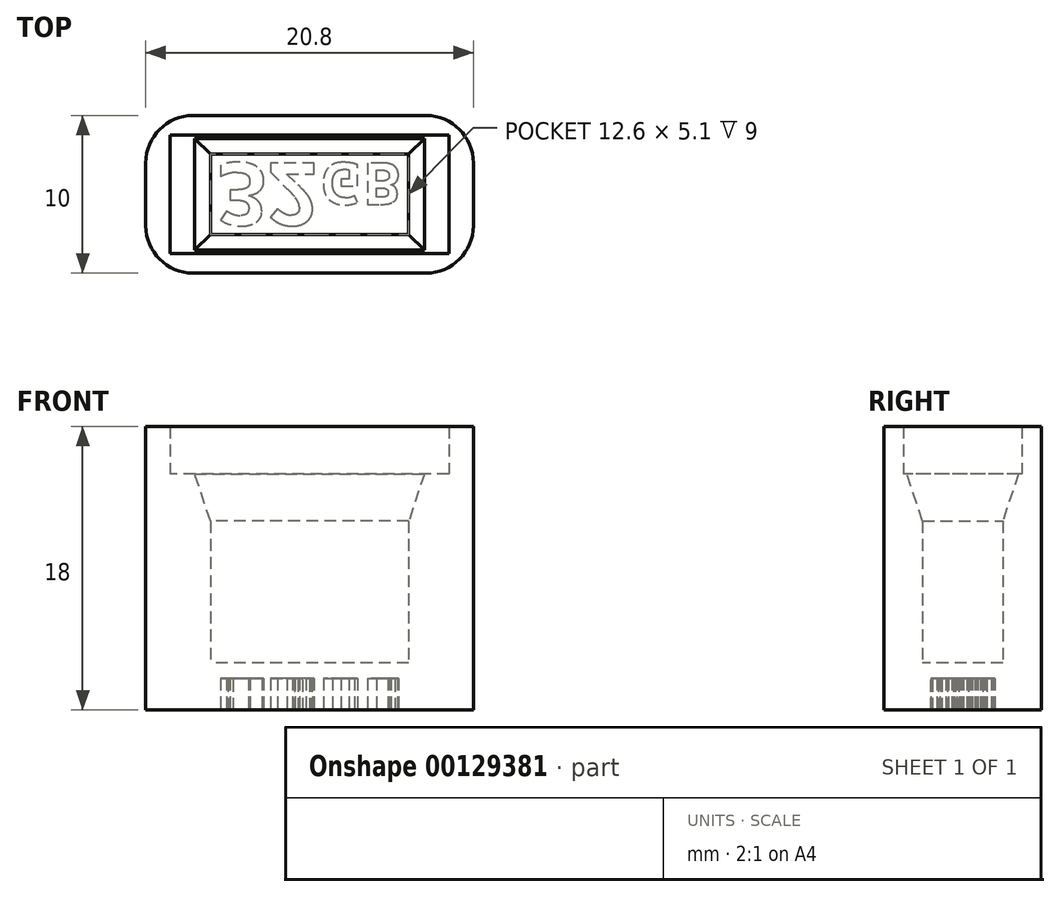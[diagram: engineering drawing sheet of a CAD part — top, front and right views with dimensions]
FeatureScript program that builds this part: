
annotation { "Feature Type Name" : "Feature", "Feature Type Description" : "" }
export const myFeature = defineFeature(function(context is Context, id is Id, definition is map)
    precondition{}
    {
        {
            var Q0;
            Q0=qCreatedBy(makeId("Top.planeOp"),FACE);
            var sketch = newSketch(context, id + "F0", { "sketchPlane" : qUnion([Q0])});
            skLineSegment(sketch, "E0.bottom", {"start": v(10.4, 5) * mm, "end": v(-10.4, 5) * mm});
            skLineSegment(sketch, "E0.top", {"start": v(10.4, -5) * mm, "end": v(-10.4, -5) * mm});
            skLineSegment(sketch, "E0.left", {"start": v(10.4, 5) * mm, "end": v(10.4, -5) * mm});
            skLineSegment(sketch, "E0.right", {"start": v(-10.4, 5) * mm, "end": v(-10.4, -5) * mm});
            skPoint(sketch, "E0.middle", {"position": v(0, 0) * mm});
            skLineSegment(sketch, "E1.bottom", {"start": v(8.85, 3.75) * mm, "end": v(-8.85, 3.75) * mm});
            skLineSegment(sketch, "E1.top", {"start": v(8.85, -3.75) * mm, "end": v(-8.85, -3.75) * mm});
            skLineSegment(sketch, "E1.left", {"start": v(8.85, 3.75) * mm, "end": v(8.85, -3.75) * mm});
            skLineSegment(sketch, "E1.right", {"start": v(-8.85, 3.75) * mm, "end": v(-8.85, -3.75) * mm});
            skSolve(sketch);
        }
        {
            var Q0;
            Q0=makeQuery(id+"F0.imprint","IMPRINT",FACE,{"disambiguationData":[TD([[makeQuery(id+"F0.imprint","IMPRINT",EDGE,{"derivedFrom":sQuery(id+"F0.wireOp",EDGE,"E0.bottom")}),1.0]])]});
            extrude(context, id + "F1", {"entities" : qUnion([Q0]), "depth" : 15 * mm});
        }
        {
            var Q0;
            Q0=makeQuery(id+"F0.imprint","IMPRINT",FACE,{"disambiguationData":[TD([[makeQuery(id+"F0.imprint","IMPRINT",EDGE,{"derivedFrom":sQuery(id+"F0.wireOp",EDGE,"E1.bottom")}),1.0]])]});
            var Q1;
            Q1=makeQuery(id+"F0.imprint","IMPRINT",FACE,{"disambiguationData":[TD([[makeQuery(id+"F0.imprint","IMPRINT",EDGE,{"derivedFrom":sQuery(id+"F0.wireOp",EDGE,"E0.bottom")}),1.0]])]});
            extrude(context, id + "F2", {"entities" : qUnion([Q0, Q1]), "operationType" : NewBodyOperationType.ADD, "oppositeDirection" : true, "depth" : 3 * mm});
        }
        {
            var Q0;
            {var subQ0=sQuery(id+"F0.wireOp",EDGE,"E0.right");var subQ1=sQuery(id+"F0.wireOp",EDGE,"E0.top");Q0=makeQuery(id+"F2.boolean.opBoolean","MERGE",EDGE,{"derivedFrom":[makeQuery(id+"F1.opExtrude","SWEPT_EDGE",EDGE,{"disambiguationData":[OSD([subQ1,subQ0])]}),makeQuery(id+"F2.opExtrude","SWEPT_EDGE",EDGE,{"disambiguationData":[OSD([subQ1,subQ0])]})]});}
            var Q1;
            {var subQ0=sQuery(id+"F0.wireOp",EDGE,"E0.right");var subQ1=sQuery(id+"F0.wireOp",EDGE,"E0.bottom");Q1=makeQuery(id+"F2.boolean.opBoolean","MERGE",EDGE,{"derivedFrom":[makeQuery(id+"F1.opExtrude","SWEPT_EDGE",EDGE,{"disambiguationData":[OSD([subQ1,subQ0])]}),makeQuery(id+"F2.opExtrude","SWEPT_EDGE",EDGE,{"disambiguationData":[OSD([subQ1,subQ0])]})]});}
            var Q2;
            {var subQ0=sQuery(id+"F0.wireOp",EDGE,"E0.left");var subQ1=sQuery(id+"F0.wireOp",EDGE,"E0.bottom");Q2=makeQuery(id+"F2.boolean.opBoolean","MERGE",EDGE,{"derivedFrom":[makeQuery(id+"F1.opExtrude","SWEPT_EDGE",EDGE,{"disambiguationData":[OSD([subQ1,subQ0])]}),makeQuery(id+"F2.opExtrude","SWEPT_EDGE",EDGE,{"disambiguationData":[OSD([subQ1,subQ0])]})]});}
            var Q3;
            {var subQ0=sQuery(id+"F0.wireOp",EDGE,"E0.left");var subQ1=sQuery(id+"F0.wireOp",EDGE,"E0.top");Q3=makeQuery(id+"F2.boolean.opBoolean","MERGE",EDGE,{"derivedFrom":[makeQuery(id+"F1.opExtrude","SWEPT_EDGE",EDGE,{"disambiguationData":[OSD([subQ1,subQ0])]}),makeQuery(id+"F2.opExtrude","SWEPT_EDGE",EDGE,{"disambiguationData":[OSD([subQ1,subQ0])]})]});}
            fillet(context, id + "F3", {"entities" : qUnion([Q0, Q1, Q2, Q3]), "radius" : 3 * mm, "tangentPropagation" : true, "allowEdgeOverflow" : false});
        }
        {
            var Q0;
            Q0=makeQuery(id+"F2.opExtrude","CAP_FACE",FACE,{"disambiguationData":[OSD([sQuery(id+"F0.wireOp",EDGE,"E0.bottom"),sQuery(id+"F0.wireOp",EDGE,"E0.top"),sQuery(id+"F0.wireOp",EDGE,"E0.left"),sQuery(id+"F0.wireOp",EDGE,"E0.right")])],"isStart":true});
            var sketch = newSketch(context, id + "F4", { "sketchPlane" : qUnion([Q0])});
            skLineSegment(sketch, "E2.bottom", {"start": v(6.3, 2.55) * mm, "end": v(-6.3, 2.55) * mm});
            skLineSegment(sketch, "E2.top", {"start": v(6.3, -2.55) * mm, "end": v(-6.3, -2.55) * mm});
            skLineSegment(sketch, "E2.left", {"start": v(6.3, 2.55) * mm, "end": v(6.3, -2.55) * mm});
            skLineSegment(sketch, "E2.right", {"start": v(-6.3, 2.55) * mm, "end": v(-6.3, -2.55) * mm});
            skPoint(sketch, "E2.middle", {"position": v(0, 0) * mm});
            skSolve(sketch);
        }
        {
            var Q0;
            Q0=makeQuery(id+"F4.imprint","IMPRINT",FACE,{"disambiguationData":[TD([[makeQuery(id+"F4.imprint","IMPRINT",EDGE,{"derivedFrom":sQuery(id+"F4.wireOp",EDGE,"E2.bottom")}),-1.0]])]});
            extrude(context, id + "F5", {"entities" : qUnion([Q0]), "operationType" : NewBodyOperationType.ADD, "depth" : 12 * mm});
        }
        {
            var Q0;
            Q0=makeQuery(id+"F5.opExtrude","CAP_EDGE",EDGE,{"disambiguationData":[OSD([sQuery(id+"F4.wireOp",EDGE,"E2.bottom")])],"isStart":false});
            var Q1;
            Q1=makeQuery(id+"F5.opExtrude","CAP_EDGE",EDGE,{"disambiguationData":[OSD([sQuery(id+"F4.wireOp",EDGE,"E2.right")])],"isStart":false});
            var Q2;
            Q2=makeQuery(id+"F5.opExtrude","CAP_EDGE",EDGE,{"disambiguationData":[OSD([sQuery(id+"F4.wireOp",EDGE,"E2.top")])],"isStart":false});
            var Q3;
            Q3=makeQuery(id+"F5.opExtrude","CAP_EDGE",EDGE,{"disambiguationData":[OSD([sQuery(id+"F4.wireOp",EDGE,"E2.left")])],"isStart":false});
            chamfer(context, id + "F6", {"entities" : qUnion([Q0, Q1, Q2, Q3]), "chamferType" : ChamferType.TWO_OFFSETS, "width1" : 3 * mm, "oppositeDirection" : false, "width2" : 1 * mm, "tangentPropagation" : true});
        }
        {
            var Q0;
            Q0=makeQuery(id+"F2.opExtrude","CAP_FACE",FACE,{"disambiguationData":[OSD([sQuery(id+"F0.wireOp",EDGE,"E0.bottom"),sQuery(id+"F0.wireOp",EDGE,"E0.top"),sQuery(id+"F0.wireOp",EDGE,"E0.left"),sQuery(id+"F0.wireOp",EDGE,"E0.right")])],"isStart":false});
            var sketch = newSketch(context, id + "F7", { "sketchPlane" : qUnion([Q0])});
            skText(sketch, "E3", { "text": "32", "fontName": "OpenSans-Bold.ttf"});
            skPoint(sketch, "E4", {"position": v(-3.91, 0) * mm});
            skText(sketch, "E5", { "text": "GB", "fontName": "OpenSans-Bold.ttf"});
            skLineSegment(sketch, "E6", {"start": v(-8.8, 0) * mm, "end": v(8.8, 0) * mm, "construction": true});
            skPoint(sketch, "E7", {"position": v(0, 0) * mm});
            const initialGuessF7  = {"E3": [-0.00587, -0.002, 1, 0, 0.004], "E5": [0.00066, -0.002, 1, 0, 0.00267]};
            skSetInitialGuess(sketch, initialGuessF7);
            skSolve(sketch);
        }
        {
            var Q0;
            Q0=makeQuery(id+"F7.imprint","IMPRINT",FACE,{"disambiguationData":[TD([[makeQuery(id+"F7.imprint","IMPRINT",EDGE,{"derivedFrom":sQuery(id+"F7.wireOp",EDGE,"E3.sketch_text.stroke-0")}),-1.0]])]});
            var Q1;
            Q1=makeQuery(id+"F7.imprint","IMPRINT",FACE,{"disambiguationData":[TD([[makeQuery(id+"F7.imprint","IMPRINT",EDGE,{"derivedFrom":sQuery(id+"F7.wireOp",EDGE,"E3.sketch_text.stroke-27")}),-1.0]])]});
            var Q2;
            Q2=makeQuery(id+"F7.imprint","IMPRINT",FACE,{"disambiguationData":[TD([[makeQuery(id+"F7.imprint","IMPRINT",EDGE,{"derivedFrom":sQuery(id+"F7.wireOp",EDGE,"E5.sketch_text.stroke-0")}),-1.0]])]});
            var Q3;
            Q3=makeQuery(id+"F7.imprint","IMPRINT",FACE,{"disambiguationData":[TD([[makeQuery(id+"F7.imprint","IMPRINT",EDGE,{"derivedFrom":sQuery(id+"F7.wireOp",EDGE,"E5.sketch_text.stroke-19")}),-1.0]])]});
            extrude(context, id + "F8", {"entities" : qUnion([Q0, Q1, Q2, Q3]), "operationType" : NewBodyOperationType.REMOVE, "oppositeDirection" : true, "depth" : 2 * mm});
        }
    });
